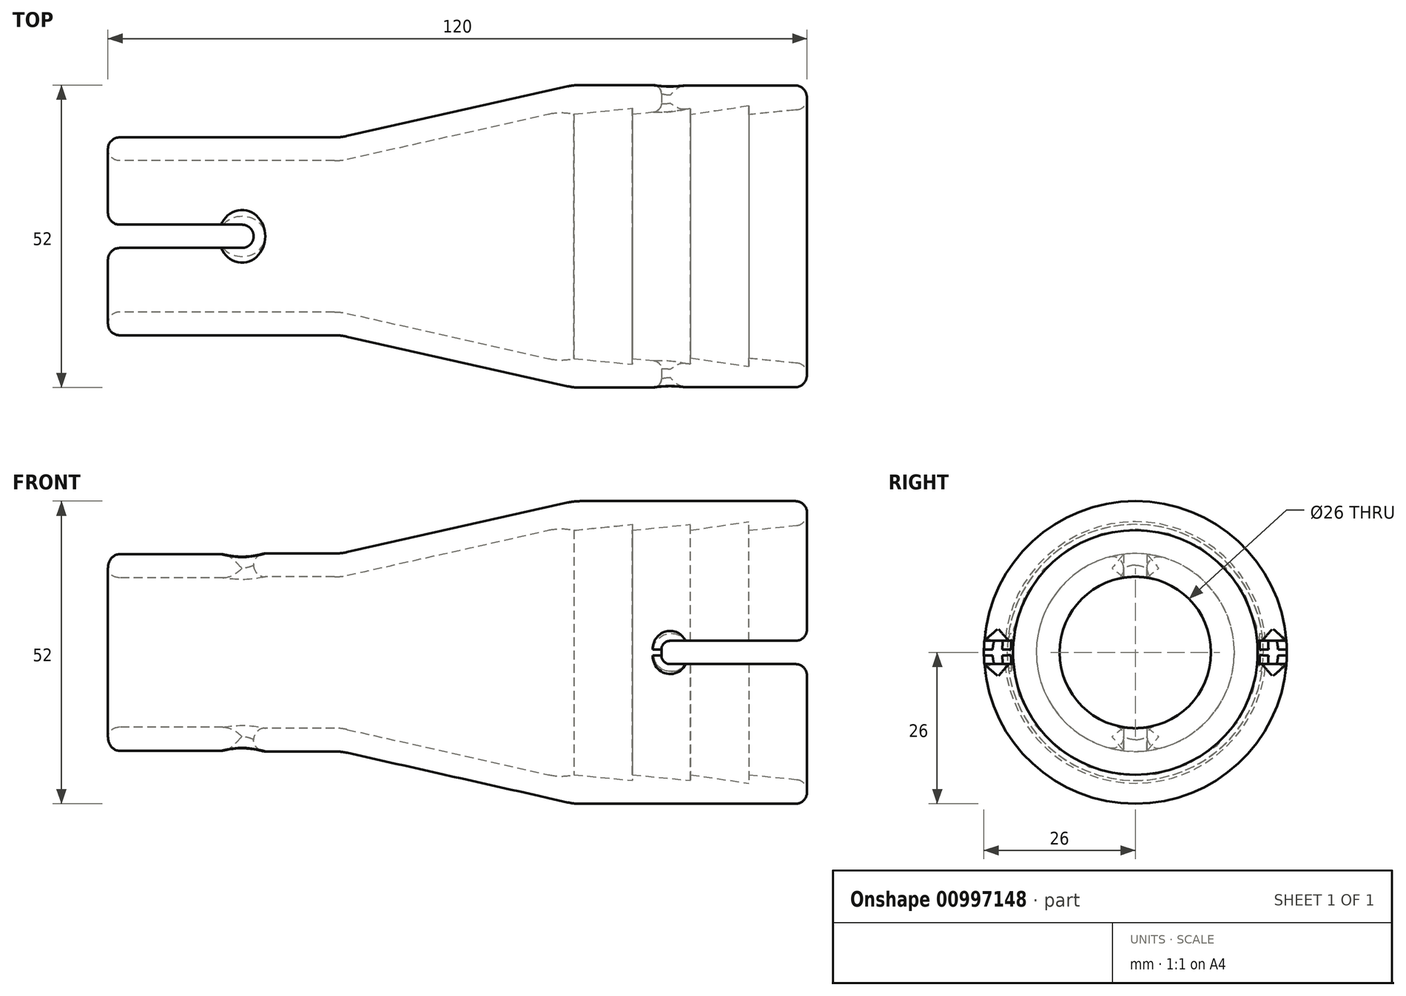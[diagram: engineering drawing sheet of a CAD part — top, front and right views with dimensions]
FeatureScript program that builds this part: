
annotation { "Feature Type Name" : "Feature", "Feature Type Description" : "" }
export const myFeature = defineFeature(function(context is Context, id is Id, definition is map)
    precondition{}
    {
        {
            var Q0;
            Q0=qCreatedBy(makeId("Top.planeOp"),FACE);
            var sketch = newSketch(context, id + "F0", { "sketchPlane" : qUnion([Q0])});
            skLineSegment(sketch, "E0", {"start": v(0, 0) * mm, "end": v(-80, 0) * mm, "construction": true});
            skLineSegment(sketch, "E1", {"start": v(-80, 0) * mm, "end": v(-80, 13) * mm, "construction": true});
            skLineSegment(sketch, "E2", {"start": v(-80, 13) * mm, "end": v(-80, 17) * mm, "construction": true});
            skLineSegment(sketch, "E3", {"start": v(-80, 0) * mm, "end": v(-40, 0) * mm, "construction": true});
            skLineSegment(sketch, "E4", {"start": v(-40, 0) * mm, "end": v(-40, 13) * mm, "construction": true});
            skLineSegment(sketch, "E5", {"start": v(-40, 13) * mm, "end": v(-40, 17) * mm, "construction": true});
            skLineSegment(sketch, "E6", {"start": v(0, 0) * mm, "end": v(40, 0) * mm, "construction": true});
            skLineSegment(sketch, "E7", {"start": v(40, 0) * mm, "end": v(40, 22) * mm, "construction": true});
            skLineSegment(sketch, "E8", {"start": v(0, 0) * mm, "end": v(0, 22) * mm, "construction": true});
            skLineSegment(sketch, "E9", {"start": v(0, 22) * mm, "end": v(0, 26) * mm, "construction": true});
            skLineSegment(sketch, "E10", {"start": v(40, 22) * mm, "end": v(40, 26) * mm, "construction": true});
            skLineSegment(sketch, "E11", {"start": v(-80, 17) * mm, "end": v(-80, 13) * mm});
            skLineSegment(sketch, "E12", {"start": v(-80, 13) * mm, "end": v(-40, 13) * mm});
            skLineSegment(sketch, "E13", {"start": v(-40, 13) * mm, "end": v(0, 22) * mm});
            skLineSegment(sketch, "E14", {"start": v(40, 22) * mm, "end": v(40, 26) * mm});
            skLineSegment(sketch, "E15", {"start": v(40, 26) * mm, "end": v(0, 26) * mm});
            skLineSegment(sketch, "E16", {"start": v(0, 26) * mm, "end": v(-40, 17) * mm});
            skLineSegment(sketch, "E17", {"start": v(-40, 17) * mm, "end": v(-80, 17) * mm});
            skLineSegment(sketch, "E18", {"start": v(-80, 0) * mm, "end": v(40, 0) * mm});
            skLineSegment(sketch, "E19", {"start": v(30, 0) * mm, "end": v(30, 28.52) * mm, "construction": true});
            skLineSegment(sketch, "E20", {"start": v(20, 0) * mm, "end": v(20, 29.03) * mm, "construction": true});
            skLineSegment(sketch, "E21", {"start": v(10, 0) * mm, "end": v(10, 27.92) * mm, "construction": true});
            skLineSegment(sketch, "E22", {"start": v(40, 22) * mm, "end": v(0, 22) * mm, "construction": true});
            skLineSegment(sketch, "E23", {"start": v(0, 21) * mm, "end": v(40, 21) * mm, "construction": true});
            skLineSegment(sketch, "E24", {"start": v(40, 22) * mm, "end": v(30, 21) * mm});
            skLineSegment(sketch, "E25", {"start": v(30, 21) * mm, "end": v(30, 22.47) * mm});
            skLineSegment(sketch, "E26", {"start": v(30, 22.47) * mm, "end": v(20, 21) * mm});
            skLineSegment(sketch, "E27", {"start": v(20, 21) * mm, "end": v(20, 22) * mm});
            skLineSegment(sketch, "E28", {"start": v(20, 22) * mm, "end": v(10, 21) * mm});
            skLineSegment(sketch, "E29", {"start": v(10, 21) * mm, "end": v(10, 22) * mm});
            skLineSegment(sketch, "E30", {"start": v(10, 22) * mm, "end": v(0, 21) * mm});
            skLineSegment(sketch, "E31", {"start": v(0, 22) * mm, "end": v(0, 21) * mm});
            skSolve(sketch);
        }
        {
            var Q0;
            Q0 = qSketchRegion(id + "F0", true);
            var Q1;
            Q1=sQuery(id+"F0.wireOp",EDGE,"E18");
            revolve(context, id + "F1", {"surfaceOperationType" : NewSurfaceOperationType.NEW, "entities" : qUnion([Q0]), "axis" : qUnion([Q1]), "revolveType" : RevolveType.FULL});
        }
        {
            var Q0;
            Q0=makeQuery(id+"F1.opRevolve","SWEPT_EDGE",EDGE,{"disambiguationData":[OSD([sQuery(id+"F0.wireOp",EDGE,"E13"),sQuery(id+"F0.wireOp",EDGE,"BBKXSeU0-TTpF-3vq2-7TaT-SrT0zSh3b63O")])]});
            var Q1;
            Q1=makeQuery(id+"F1.opRevolve","SWEPT_EDGE",EDGE,{"disambiguationData":[OSD([sQuery(id+"F0.wireOp",EDGE,"E12"),sQuery(id+"F0.wireOp",EDGE,"E13")])]});
            var Q2;
            Q2=makeQuery(id+"F1.opRevolve","SWEPT_EDGE",EDGE,{"disambiguationData":[OSD([sQuery(id+"F0.wireOp",EDGE,"E15"),sQuery(id+"F0.wireOp",EDGE,"E16")])]});
            var Q3;
            Q3=makeQuery(id+"F1.opRevolve","SWEPT_EDGE",EDGE,{"disambiguationData":[OSD([sQuery(id+"F0.wireOp",EDGE,"E16"),sQuery(id+"F0.wireOp",EDGE,"E17")])]});
            fillet(context, id + "F2", {"entities" : qUnion([Q0, Q1, Q2, Q3]), "radius" : 10 * mm, "tangentPropagation" : true, "allowEdgeOverflow" : false});
        }
        {
            var Q0;
            Q0=makeQuery(id+"F1.opRevolve","SWEPT_FACE",FACE,{"disambiguationData":[OSD([sQuery(id+"F0.wireOp",EDGE,"E14")])]});
            var sketch = newSketch(context, id + "F3", { "sketchPlane" : qUnion([Q0])});
            skLineSegment(sketch, "E32.bottom", {"start": v(28.45, 2) * mm, "end": v(-28.45, 2) * mm});
            skLineSegment(sketch, "E32.top", {"start": v(28.45, -2) * mm, "end": v(-28.45, -2) * mm});
            skLineSegment(sketch, "E32.left", {"start": v(28.45, 2) * mm, "end": v(28.45, -2) * mm});
            skLineSegment(sketch, "E32.right", {"start": v(-28.45, 2) * mm, "end": v(-28.45, -2) * mm});
            skPoint(sketch, "E32.middle", {"position": v(0, 0) * mm});
            skSolve(sketch);
        }
        {
            var Q0;
            Q0 = qSketchRegion(id + "F3", true);
            extrude(context, id + "F4", {"entities" : qUnion([Q0]), "operationType" : NewBodyOperationType.REMOVE, "oppositeDirection" : true, "depth" : 25 * mm, "offsetDistance" : 25 * mm});
        }
        {
            var Q0;
            Q0=makeQuery(id+"F1.opRevolve","SWEPT_FACE",FACE,{"disambiguationData":[OSD([sQuery(id+"F0.wireOp",EDGE,"E11")])]});
            var sketch = newSketch(context, id + "F5", { "sketchPlane" : qUnion([Q0])});
            skLineSegment(sketch, "E33.bottom", {"start": v(2, 24.8) * mm, "end": v(-2, 24.8) * mm});
            skLineSegment(sketch, "E33.top", {"start": v(2, -24.8) * mm, "end": v(-2, -24.8) * mm});
            skLineSegment(sketch, "E33.left", {"start": v(2, 24.8) * mm, "end": v(2, -24.8) * mm});
            skLineSegment(sketch, "E33.right", {"start": v(-2, 24.8) * mm, "end": v(-2, -24.8) * mm});
            skPoint(sketch, "E33.middle", {"position": v(0, 0) * mm});
            skSolve(sketch);
        }
        {
            var Q0;
            Q0 = qSketchRegion(id + "F5", true);
            extrude(context, id + "F6", {"entities" : qUnion([Q0]), "operationType" : NewBodyOperationType.REMOVE, "oppositeDirection" : true, "depth" : 25 * mm, "offsetDistance" : 25 * mm});
        }
        {
            var Q0;
            Q0=makeQuery(id+"F6.boolean.opBoolean","SPLIT",FACE,{"disambiguationData":[TD([makeQuery(id+"F6.opExtrude","SWEPT_FACE",FACE,{"disambiguationData":[OSD([sQuery(id+"F5.wireOp",EDGE,"E33.left")])]})])],"derivedFrom":makeQuery(id+"F1.opRevolve","SWEPT_FACE",FACE,{"disambiguationData":[OSD([sQuery(id+"F0.wireOp",EDGE,"E11")])]})});
            var Q1;
            Q1=makeQuery(id+"F6.boolean.opBoolean","SPLIT",FACE,{"disambiguationData":[TD([makeQuery(id+"F6.opExtrude","SWEPT_FACE",FACE,{"disambiguationData":[OSD([sQuery(id+"F5.wireOp",EDGE,"E33.right")])]})])],"derivedFrom":makeQuery(id+"F1.opRevolve","SWEPT_FACE",FACE,{"disambiguationData":[OSD([sQuery(id+"F0.wireOp",EDGE,"E11")])]})});
            var Q2;
            Q2=makeQuery(id+"F6.boolean.opBoolean","COPY",FACE,{"disambiguationData":[OD(1.0)],"derivedFrom":makeQuery(id+"F6.opExtrude","CAP_FACE",FACE,{"disambiguationData":[OSD([sQuery(id+"F5.wireOp",EDGE,"E33.bottom"),sQuery(id+"F5.wireOp",EDGE,"E33.top"),sQuery(id+"F5.wireOp",EDGE,"E33.left"),sQuery(id+"F5.wireOp",EDGE,"E33.right")])],"isStart":false})});
            var Q3;
            Q3=makeQuery(id+"F6.boolean.opBoolean","COPY",FACE,{"disambiguationData":[OD(0.0)],"derivedFrom":makeQuery(id+"F6.opExtrude","CAP_FACE",FACE,{"disambiguationData":[OSD([sQuery(id+"F5.wireOp",EDGE,"E33.bottom"),sQuery(id+"F5.wireOp",EDGE,"E33.top"),sQuery(id+"F5.wireOp",EDGE,"E33.left"),sQuery(id+"F5.wireOp",EDGE,"E33.right")])],"isStart":false})});
            var Q4;
            Q4=makeQuery(id+"F4.boolean.opBoolean","SPLIT",FACE,{"disambiguationData":[TD([makeQuery(id+"F4.opExtrude","SWEPT_FACE",FACE,{"disambiguationData":[OSD([sQuery(id+"F3.wireOp",EDGE,"E32.top")])]})])],"derivedFrom":makeQuery(id+"F1.opRevolve","SWEPT_FACE",FACE,{"disambiguationData":[OSD([sQuery(id+"F0.wireOp",EDGE,"E14")])]})});
            var Q5;
            Q5=makeQuery(id+"F4.boolean.opBoolean","SPLIT",FACE,{"disambiguationData":[TD([makeQuery(id+"F4.opExtrude","SWEPT_FACE",FACE,{"disambiguationData":[OSD([sQuery(id+"F3.wireOp",EDGE,"E32.bottom")])]})])],"derivedFrom":makeQuery(id+"F1.opRevolve","SWEPT_FACE",FACE,{"disambiguationData":[OSD([sQuery(id+"F0.wireOp",EDGE,"E14")])]})});
            fillet(context, id + "F7", {"entities" : qUnion([Q0, Q1, Q2, Q3, Q4, Q5]), "tangentPropagation" : true, "radius" : 2 * mm, "defaultsChanged" : false, "vertexSettings" : [], "allowEdgeOverflow" : false});
        }
        {
            var Q0;
            Q0=makeQuery(id+"F4.boolean.opBoolean","COPY",FACE,{"disambiguationData":[OD(1.0)],"derivedFrom":makeQuery(id+"F4.opExtrude","CAP_FACE",FACE,{"disambiguationData":[OSD([sQuery(id+"F3.wireOp",EDGE,"E32.bottom"),sQuery(id+"F3.wireOp",EDGE,"E32.top"),sQuery(id+"F3.wireOp",EDGE,"E32.left"),sQuery(id+"F3.wireOp",EDGE,"E32.right")])],"isStart":false})});
            var Q1;
            Q1=makeQuery(id+"F4.boolean.opBoolean","COPY",FACE,{"disambiguationData":[OD(0.0)],"derivedFrom":makeQuery(id+"F4.opExtrude","CAP_FACE",FACE,{"disambiguationData":[OSD([sQuery(id+"F3.wireOp",EDGE,"E32.bottom"),sQuery(id+"F3.wireOp",EDGE,"E32.top"),sQuery(id+"F3.wireOp",EDGE,"E32.left"),sQuery(id+"F3.wireOp",EDGE,"E32.right")])],"isStart":false})});
            fillet(context, id + "F8", {"entities" : qUnion([Q0, Q1]), "tangentPropagation" : true, "radius" : 1.5 * mm, "defaultsChanged" : true, "vertexSettings" : [], "allowEdgeOverflow" : false});
        }
    });
